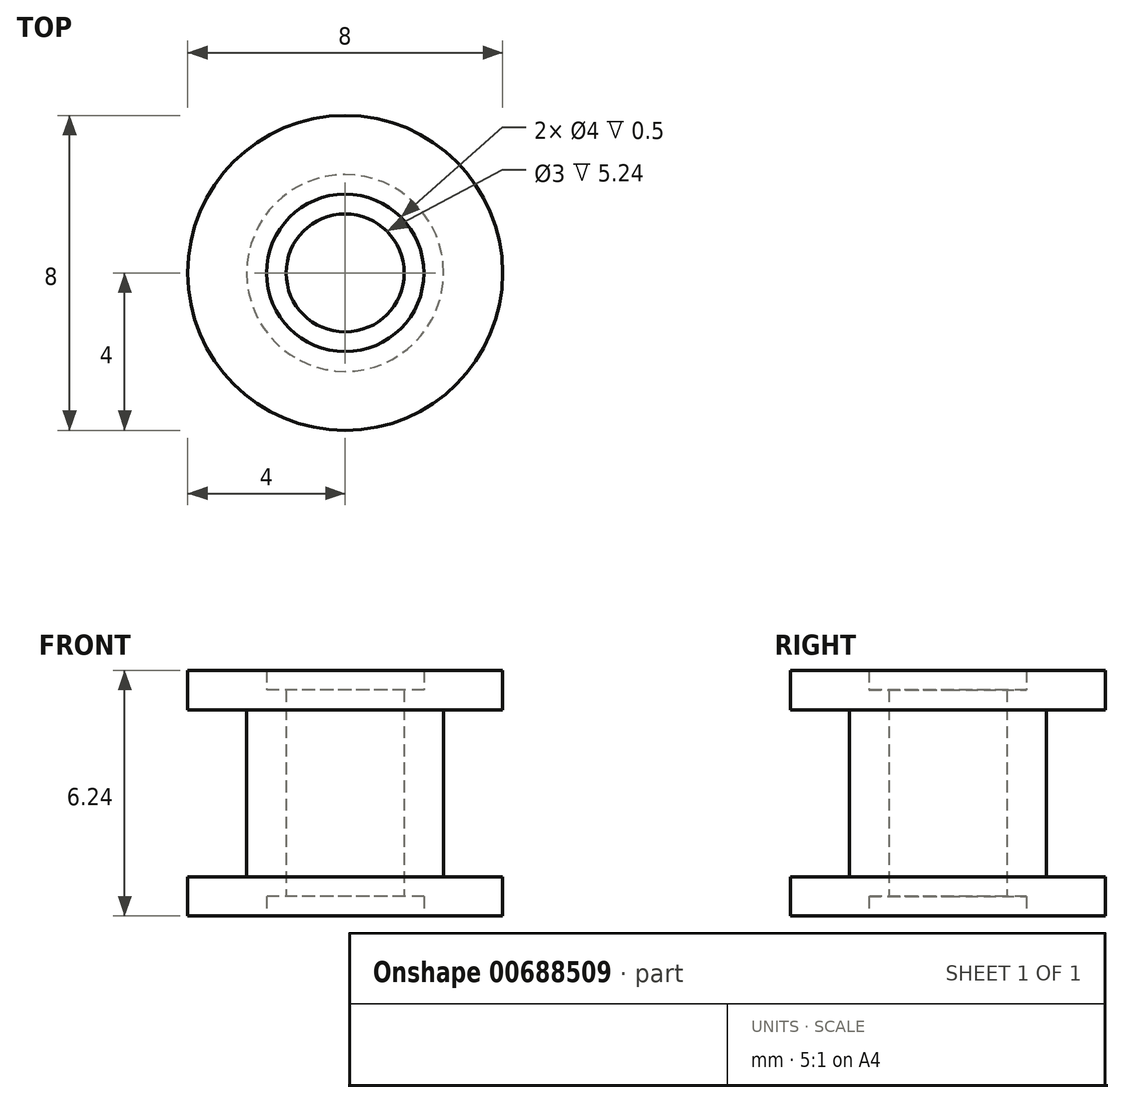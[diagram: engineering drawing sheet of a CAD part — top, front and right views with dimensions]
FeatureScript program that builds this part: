
annotation { "Feature Type Name" : "Feature", "Feature Type Description" : "" }
export const myFeature = defineFeature(function(context is Context, id is Id, definition is map)
    precondition{}
    {
        {
            var Q0;
            Q0=qCreatedBy(makeId("Top.planeOp"),FACE);
            var sketch = newSketch(context, id + "F0", { "sketchPlane" : qUnion([Q0])});
            skCircle(sketch, "E0", {"center": v(0, 0) * mm, "radius": 4 * mm});
            skCircle(sketch, "E1", {"center": v(0, 0) * mm, "radius": 2 * mm});
            skSolve(sketch);
        }
        {
            var Q0;
            Q0=qCreatedBy(makeId("Top.planeOp"),FACE);
            cPlane(context, id + "F1", {"entities" : qUnion([Q0]), "cplaneType" : CPlaneType.OFFSET, "offset" : 2.62 * mm, "width" : 152.4 * mm, "height" : 152.4 * mm});
        }
        {
            var Q0;
            Q0=qCreatedBy(id+"F1.planeOp",FACE);
            var sketch = newSketch(context, id + "F2", { "sketchPlane" : qUnion([Q0])});
            skCircle(sketch, "E2", {"center": v(0, 0) * mm, "radius": 2.5 * mm});
            skCircle(sketch, "E3", {"center": v(0, 0) * mm, "radius": 1.5 * mm});
            skSolve(sketch);
        }
        {
            var Q0;
            Q0=qCreatedBy(id+"F1.planeOp",FACE);
            cPlane(context, id + "F3", {"entities" : qUnion([Q0]), "cplaneType" : CPlaneType.OFFSET, "offset" : 2.62 * mm, "width" : 152.4 * mm, "height" : 152.4 * mm});
        }
        {
            var Q0;
            Q0=qCreatedBy(id+"F3.planeOp",FACE);
            var sketch = newSketch(context, id + "F4", { "sketchPlane" : qUnion([Q0])});
            skCircle(sketch, "E4", {"center": v(0, 0) * mm, "radius": 2 * mm});
            skCircle(sketch, "E5", {"center": v(0, 0) * mm, "radius": 4 * mm});
            skSolve(sketch);
        }
        {
            var Q0;
            Q0=qSketchRegion(id+"F0",true);
            extrude(context, id + "F5", {"entities" : qUnion([Q0]), "endBound" : BoundingType.SYMMETRIC, "depth" : 1 * mm, "offsetDistance" : 25.4 * mm});
        }
        {
            var Q0;
            Q0=qSketchRegion(id+"F2",true);
            extrude(context, id + "F6", {"entities" : qUnion([Q0]), "operationType" : NewBodyOperationType.ADD, "endBound" : BoundingType.SYMMETRIC, "depth" : 5.24 * mm, "offsetDistance" : 25.4 * mm});
        }
        {
            var Q0;
            Q0=qSketchRegion(id+"F4",true);
            extrude(context, id + "F7", {"entities" : qUnion([Q0]), "operationType" : NewBodyOperationType.ADD, "endBound" : BoundingType.SYMMETRIC, "depth" : 1 * mm, "offsetDistance" : 25.4 * mm});
        }
    });
